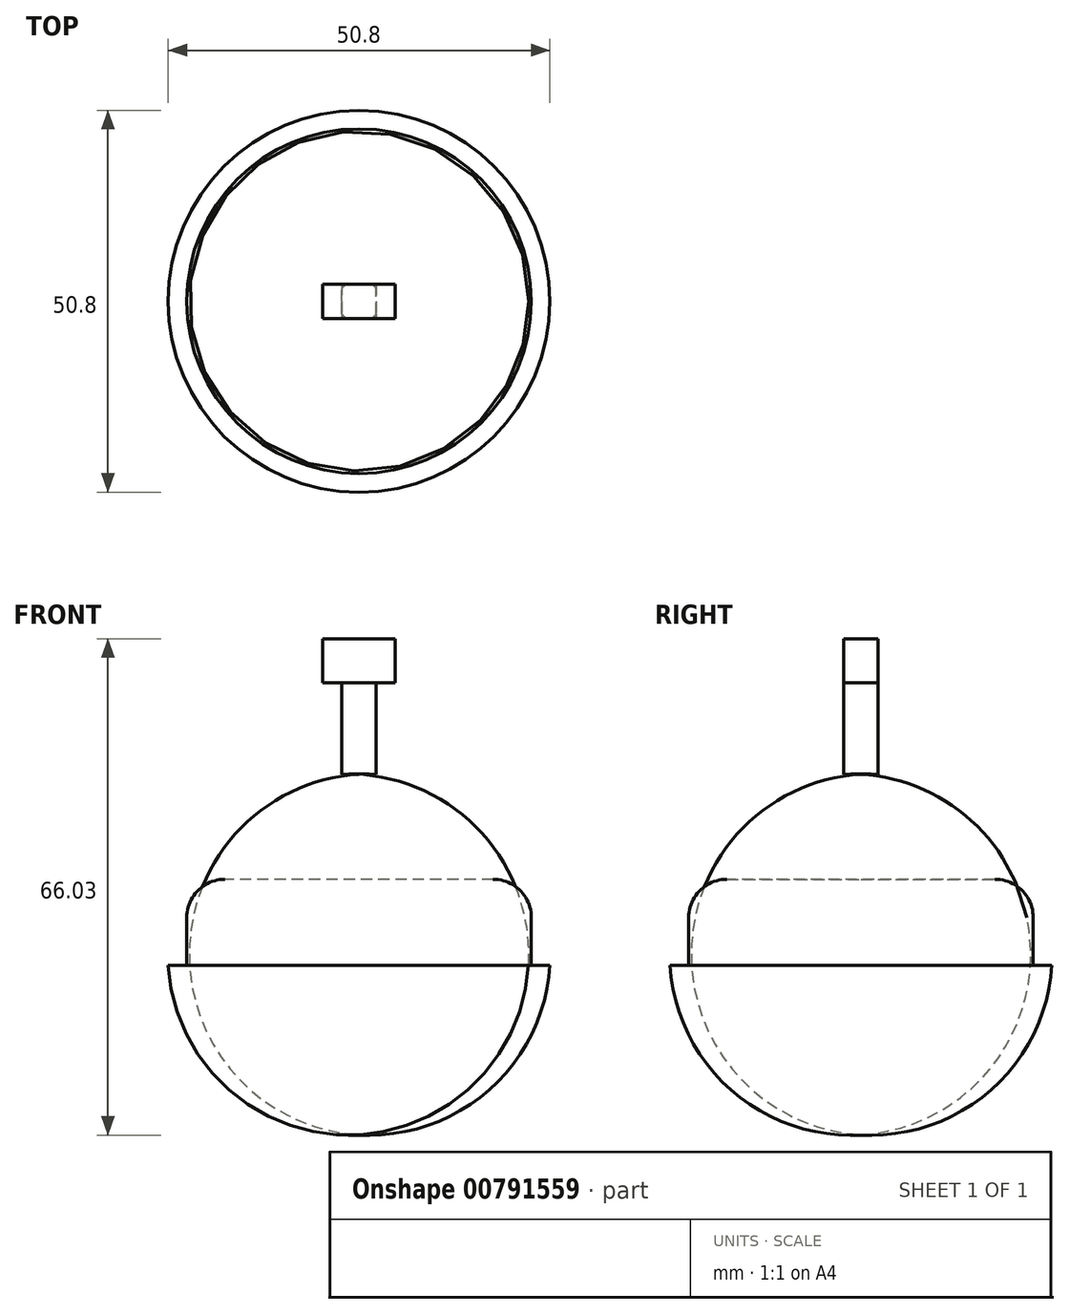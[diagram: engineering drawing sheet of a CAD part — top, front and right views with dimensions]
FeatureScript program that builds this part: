
annotation { "Feature Type Name" : "Feature", "Feature Type Description" : "" }
export const myFeature = defineFeature(function(context is Context, id is Id, definition is map)
    precondition{}
    {
        {
            var Q0;
            Q0=qCreatedBy(makeId("Front.planeOp"),FACE);
            var sketch = newSketch(context, id + "F0", { "sketchPlane" : qUnion([Q0])});
            skLineSegment(sketch, "E0", {"start": v(0, 0) * mm, "end": v(25.4, 0) * mm});
            skLineSegment(sketch, "E1", {"start": v(0, 0) * mm, "end": v(0, 25.4) * mm});
            skArc(sketch, "E2", {"start": v(25.4, 0) * mm, "mid": v(18.4, 18.4) * mm, "end": v(0, 25.4) * mm});
            skSolve(sketch);
        }
        {
            var Q0;
            Q0 = qSketchRegion(id + "F0", true);
            var Q1;
            Q1=sQuery(id+"F0.wireOp",EDGE,"E1");
            revolve(context, id + "F1", {"surfaceOperationType" : NewSurfaceOperationType.NEW, "entities" : qUnion([Q0]), "axis" : qUnion([Q1]), "revolveType" : RevolveType.FULL});
        }
        {
            var Q0;
            Q0=qCreatedBy(makeId("Top.planeOp"),FACE);
            var sketch = newSketch(context, id + "F2", { "sketchPlane" : qUnion([Q0])});
            skLineSegment(sketch, "E3", {"start": v(-25.47, 0) * mm, "end": v(-22.93, 0) * mm});
            skCircle(sketch, "E4", {"center": v(0, 0) * mm, "radius": 22.93 * mm});
            skSolve(sketch);
        }
        {
            var Q0;
            Q0 = qSketchRegion(id + "F2", true);
            extrude(context, id + "F3", {"entities" : qUnion([Q0]), "operationType" : NewBodyOperationType.REMOVE, "depth" : 11.43 * mm, "offsetDistance" : 25.4 * mm});
        }
        {
            var Q0;
            Q0=makeQuery(id+"F3.boolean.opBoolean","COPY",EDGE,{"derivedFrom":makeQuery(id+"F3.opExtrude","CAP_EDGE",EDGE,{"disambiguationData":[OSD([sQuery(id+"F2.wireOp",EDGE,"E4")])],"isStart":false})});
            fillet(context, id + "F4", {"entities" : qUnion([Q0]), "radius" : 5.08 * mm, "tangentPropagation" : true, "allowEdgeOverflow" : false});
        }
        {
            var Q0;
            Q0=qCreatedBy(makeId("Top.planeOp"),FACE);
            var sketch = newSketch(context, id + "F5", { "sketchPlane" : qUnion([Q0])});
            skPoint(sketch, "E5.middle", {"position": v(0, 0) * mm});
            skLineSegment(sketch, "E6.bottom", {"start": v(-2.29, 2.29) * mm, "end": v(2.29, 2.29) * mm});
            skLineSegment(sketch, "E6.top", {"start": v(-2.29, -2.29) * mm, "end": v(2.29, -2.29) * mm});
            skLineSegment(sketch, "E6.left", {"start": v(-2.29, 2.29) * mm, "end": v(-2.29, -2.29) * mm});
            skLineSegment(sketch, "E6.right", {"start": v(2.29, 2.29) * mm, "end": v(2.29, -2.29) * mm});
            skSolve(sketch);
        }
        {
            var Q0;
            Q0 = qSketchRegion(id + "F5", true);
            extrude(context, id + "F6", {"entities" : qUnion([Q0]), "operationType" : NewBodyOperationType.ADD, "depth" : 37.6 * mm, "offsetDistance" : 25.4 * mm, "hasSecondDirection" : true, "secondDirectionOppositeDirection" : false, "secondDirectionDepth" : 25.4 * mm});
        }
        {
            var Q0;
            Q0=qCreatedBy(makeId("Top.planeOp"),FACE);
            var sketch = newSketch(context, id + "F7", { "sketchPlane" : qUnion([Q0])});
            skLineSegment(sketch, "E7", {"start": v(0, -2.3) * mm, "end": v(-4.83, -2.3) * mm});
            skLineSegment(sketch, "E8", {"start": v(0, -2.3) * mm, "end": v(4.83, -2.3) * mm});
            skLineSegment(sketch, "E9", {"start": v(4.83, -2.3) * mm, "end": v(4.83, 2.27) * mm});
            skLineSegment(sketch, "E10", {"start": v(-4.83, -2.3) * mm, "end": v(-4.83, 2.27) * mm});
            skLineSegment(sketch, "E11", {"start": v(-4.83, 2.27) * mm, "end": v(4.83, 2.27) * mm});
            skSolve(sketch);
        }
        {
            var Q0;
            Q0 = qSketchRegion(id + "F7", true);
            extrude(context, id + "F8", {"entities" : qUnion([Q0]), "operationType" : NewBodyOperationType.ADD, "depth" : 43.43 * mm, "offsetDistance" : 25.4 * mm, "hasSecondDirection" : true, "secondDirectionOppositeDirection" : false, "secondDirectionDepth" : 37.6 * mm});
        }
    });
